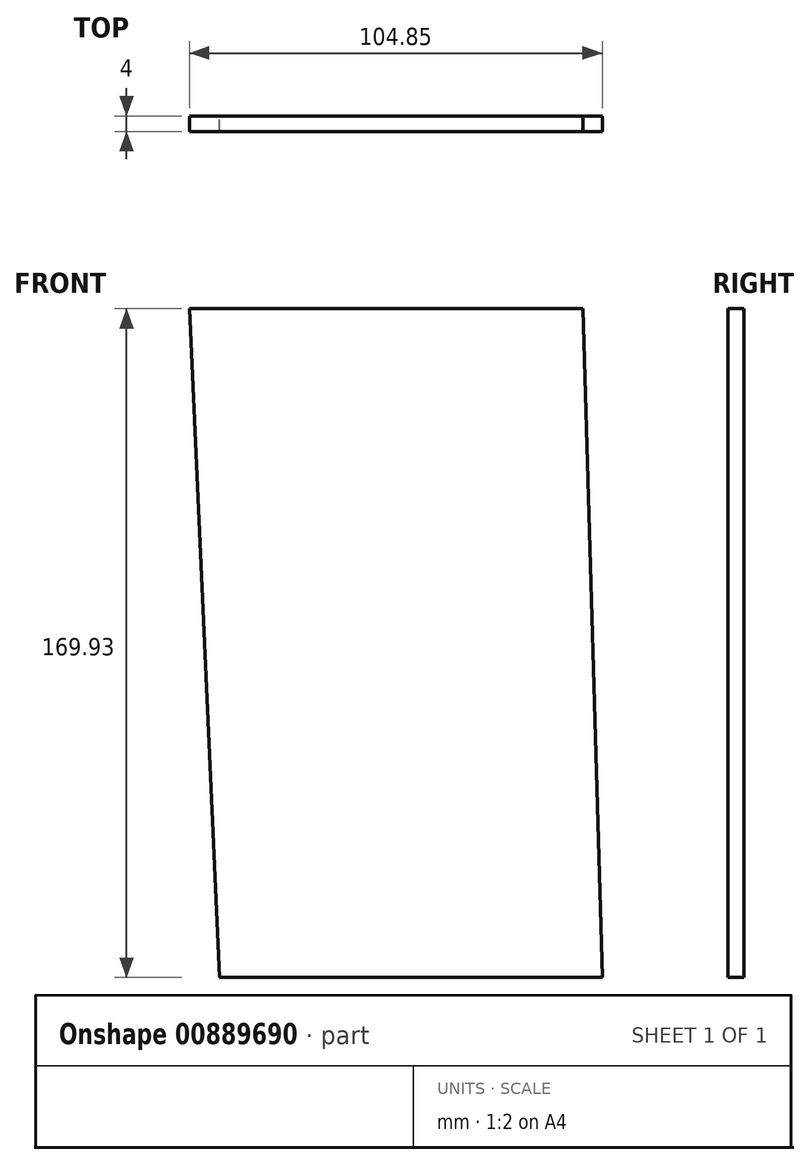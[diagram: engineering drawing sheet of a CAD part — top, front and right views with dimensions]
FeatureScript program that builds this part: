
annotation { "Feature Type Name" : "Feature", "Feature Type Description" : "" }
export const myFeature = defineFeature(function(context is Context, id is Id, definition is map)
    precondition{}
    {
        {
            var Q0;
            Q0=qCreatedBy(makeId("Front.planeOp"),FACE);
            var sketch = newSketch(context, id + "F0", { "sketchPlane" : qUnion([Q0])});
            skLineSegment(sketch, "E0", {"start": v(-55.56, 63.81) * mm, "end": v(44.44, 63.81) * mm});
            skLineSegment(sketch, "E1", {"start": v(44.44, 63.81) * mm, "end": v(49.3, -106.12) * mm});
            skLineSegment(sketch, "E2", {"start": v(49.3, -106.12) * mm, "end": v(-47.91, -106.12) * mm});
            skLineSegment(sketch, "E3", {"start": v(-47.91, -106.12) * mm, "end": v(-55.56, 63.81) * mm});
            skSolve(sketch);
        }
        {
            var Q0;
            Q0 = qSketchRegion(id + "F0", true);
            extrude(context, id + "F1", {"entities" : qUnion([Q0]), "depth" : 4 * mm, "offsetDistance" : 25.4 * mm});
        }
    });
